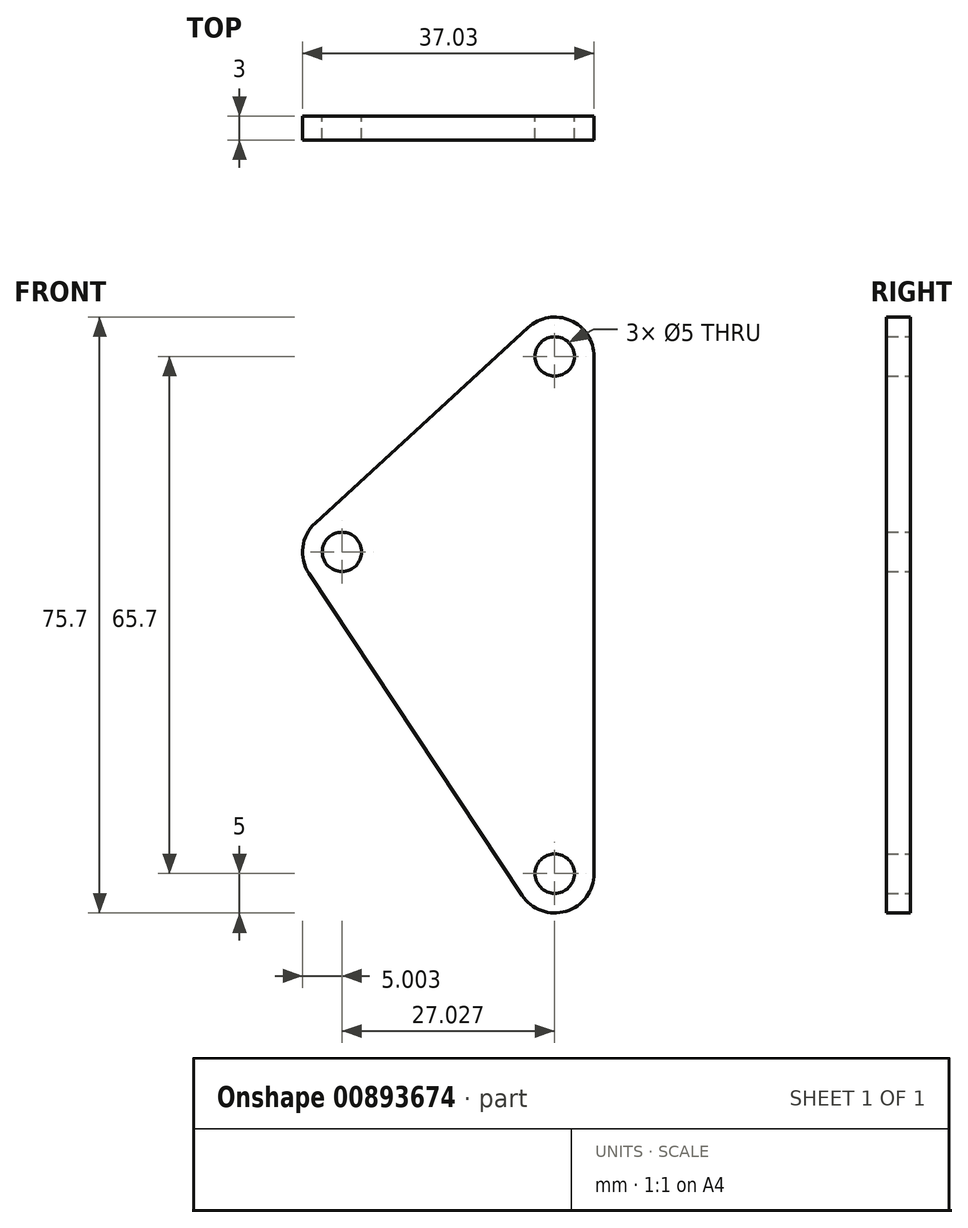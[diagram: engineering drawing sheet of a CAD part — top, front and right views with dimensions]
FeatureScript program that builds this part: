
annotation { "Feature Type Name" : "Feature", "Feature Type Description" : "" }
export const myFeature = defineFeature(function(context is Context, id is Id, definition is map)
    precondition{}
    {
        {
            var Q0;
            Q0=qCreatedBy(makeId("Front.planeOp"),FACE);
            var sketch = newSketch(context, id + "F0", { "sketchPlane" : qUnion([Q0])});
            skCircle(sketch, "E0", {"center": v(0, 65.7) * mm, "radius": 2.5 * mm});
            skCircle(sketch, "E1", {"center": v(0, 0) * mm, "radius": 2.5 * mm});
            skCircle(sketch, "E2", {"center": v(-27.03, 40.87) * mm, "radius": 2.5 * mm});
            skLineSegment(sketch, "E3", {"start": v(5, 0) * mm, "end": v(5, 65.7) * mm});
            skLineSegment(sketch, "E4", {"start": v(-3.38, 69.38) * mm, "end": v(-30.4, 44.55) * mm});
            skLineSegment(sketch, "E5", {"start": v(-31.2, 38.11) * mm, "end": v(-4.17, -2.76) * mm});
            skArc(sketch, "E6", {"start": v(-30.4, 44.55) * mm, "mid": v(-32, 41.48) * mm, "end": v(-31.2, 38.11) * mm});
            skArc(sketch, "E7", {"start": v(-4.17, -2.76) * mm, "mid": v(1.44, -4.79) * mm, "end": v(5, 0) * mm});
            skArc(sketch, "E8", {"start": v(5, 65.7) * mm, "mid": v(2.01, 70.28) * mm, "end": v(-3.38, 69.38) * mm});
            skSolve(sketch);
        }
        {
            var Q0;
            Q0 = qSketchRegion(id + "F0", true);
            extrude(context, id + "F1", {"entities" : qUnion([Q0]), "depth" : 3 * mm, "offsetDistance" : 25 * mm});
        }
    });
